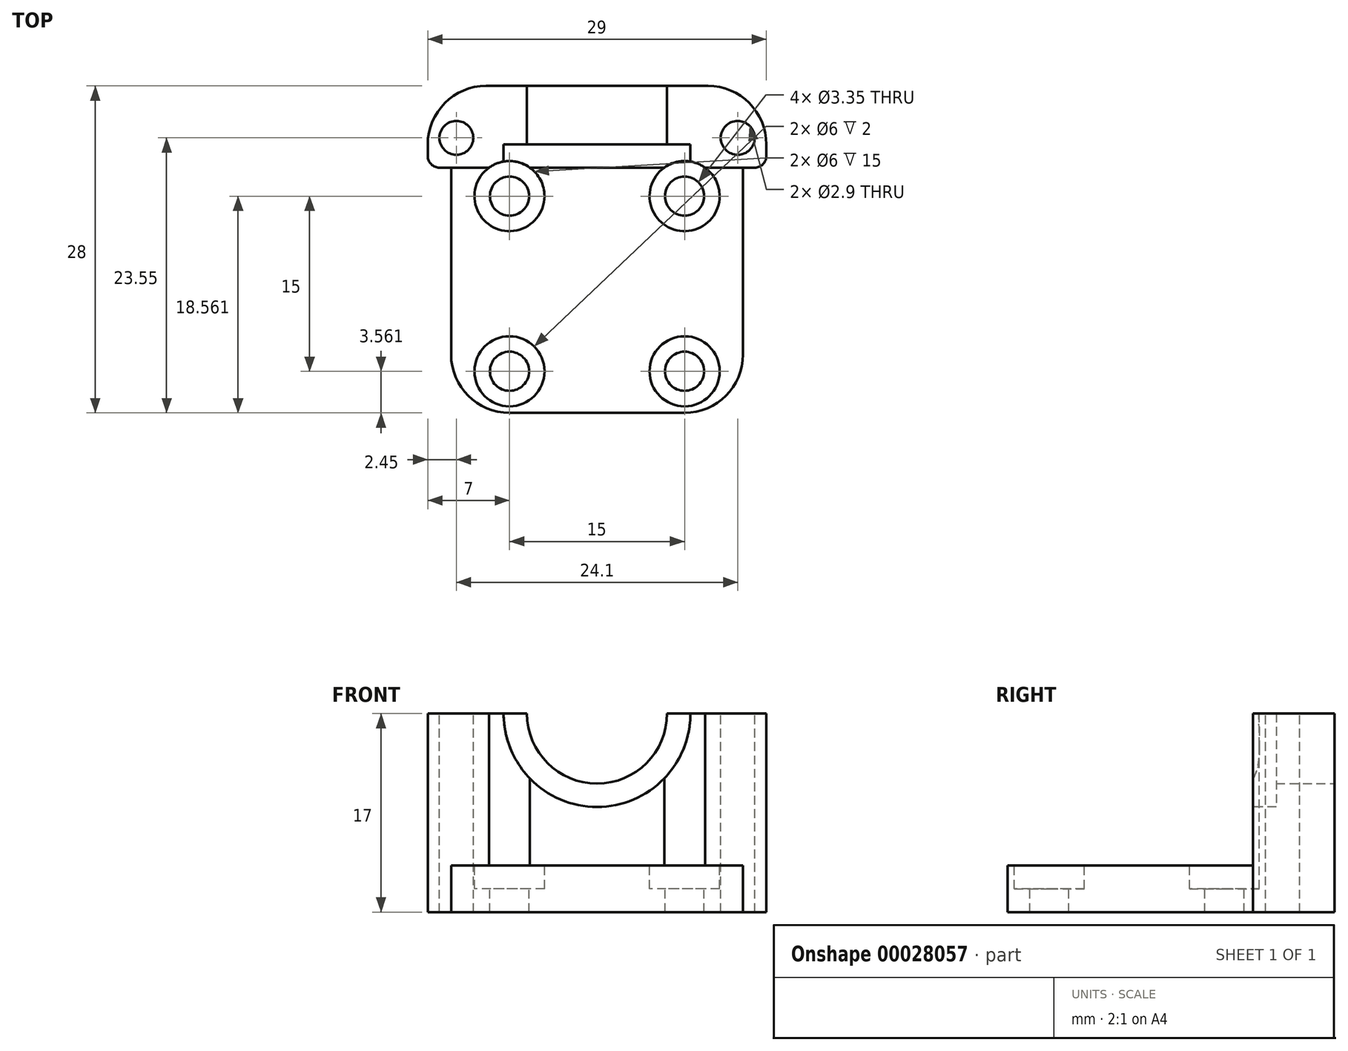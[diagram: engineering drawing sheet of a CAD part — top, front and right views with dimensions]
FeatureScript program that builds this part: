
annotation { "Feature Type Name" : "Feature", "Feature Type Description" : "" }
export const myFeature = defineFeature(function(context is Context, id is Id, definition is map)
    precondition{}
    {
        {
            var Q0;
            Q0=qCreatedBy(makeId("Top.planeOp"),FACE);
            var sketch = newSketch(context, id + "F0", { "sketchPlane" : qUnion([Q0])});
            skLineSegment(sketch, "E0.bottom", {"start": v(0, 0) * mm, "end": v(25, 0) * mm});
            skLineSegment(sketch, "E0.top", {"start": v(0, 28) * mm, "end": v(25, 28) * mm});
            skLineSegment(sketch, "E0.left", {"start": v(0, 0) * mm, "end": v(0, 28) * mm});
            skLineSegment(sketch, "E0.right", {"start": v(25, 0) * mm, "end": v(25, 28) * mm});
            skSolve(sketch);
        }
        {
            var Q0;
            Q0=qSketchRegion(id+"F0",true);
            extrude(context, id + "F1", {"entities" : qUnion([Q0]), "depth" : 4 * mm});
        }
        {
            var Q0;
            Q0=makeQuery(id+"F1.opExtrude","CAP_FACE",FACE,{"disambiguationData":[OSD([sQuery(id+"F0.wireOp",EDGE,"E0.bottom"),sQuery(id+"F0.wireOp",EDGE,"E0.top"),sQuery(id+"F0.wireOp",EDGE,"E0.left"),sQuery(id+"F0.wireOp",EDGE,"E0.right")])],"isStart":false});
            var sketch = newSketch(context, id + "F2", { "sketchPlane" : qUnion([Q0])});
            skCircle(sketch, "E1", {"center": v(5, 18.56) * mm, "radius": 1.68 * mm});
            skCircle(sketch, "E2", {"center": v(20, 18.56) * mm, "radius": 1.68 * mm});
            skCircle(sketch, "E3", {"center": v(5, 3.56) * mm, "radius": 1.68 * mm});
            skCircle(sketch, "E4", {"center": v(20, 3.56) * mm, "radius": 1.68 * mm});
            skLineSegment(sketch, "E5", {"start": v(5, 18.56) * mm, "end": v(0, 18.56) * mm});
            skLineSegment(sketch, "E6", {"start": v(20, 3.56) * mm, "end": v(25, 3.56) * mm});
            skCircle(sketch, "E7", {"center": v(5, 18.56) * mm, "radius": 3 * mm});
            skCircle(sketch, "E8", {"center": v(20, 18.56) * mm, "radius": 3 * mm});
            skCircle(sketch, "E9", {"center": v(5, 3.56) * mm, "radius": 3 * mm});
            skCircle(sketch, "E10", {"center": v(20, 3.56) * mm, "radius": 3 * mm});
            skSolve(sketch);
        }
        {
            var Q0;
            Q0=makeQuery(id+"F2.imprint","IMPRINT",FACE,{"disambiguationData":[TD([[makeQuery(id+"F2.imprint","IMPRINT",EDGE,{"derivedFrom":sQuery(id+"F2.wireOp",EDGE,"E1")}),1.0]])]});
            var Q1;
            Q1=makeQuery(id+"F2.imprint","IMPRINT",FACE,{"disambiguationData":[TD([[makeQuery(id+"F2.imprint","IMPRINT",EDGE,{"derivedFrom":sQuery(id+"F2.wireOp",EDGE,"E2")}),1.0]])]});
            var Q2;
            Q2=makeQuery(id+"F2.imprint","IMPRINT",FACE,{"disambiguationData":[TD([[makeQuery(id+"F2.imprint","IMPRINT",EDGE,{"derivedFrom":sQuery(id+"F2.wireOp",EDGE,"E4")}),1.0]])]});
            var Q3;
            Q3=makeQuery(id+"F2.imprint","IMPRINT",FACE,{"disambiguationData":[TD([[makeQuery(id+"F2.imprint","IMPRINT",EDGE,{"derivedFrom":sQuery(id+"F2.wireOp",EDGE,"E3")}),1.0]])]});
            extrude(context, id + "F3", {"entities" : qUnion([Q0, Q1, Q2, Q3]), "operationType" : NewBodyOperationType.REMOVE, "oppositeDirection" : true, "depth" : 25 * mm});
        }
        {
            var Q0;
            Q0=makeQuery(id+"F1.opExtrude","CAP_FACE",FACE,{"disambiguationData":[OSD([sQuery(id+"F0.wireOp",EDGE,"E0.bottom"),sQuery(id+"F0.wireOp",EDGE,"E0.top"),sQuery(id+"F0.wireOp",EDGE,"E0.left"),sQuery(id+"F0.wireOp",EDGE,"E0.right")])],"isStart":false});
            var sketch = newSketch(context, id + "F4", { "sketchPlane" : qUnion([Q0])});
            skLineSegment(sketch, "E11.bottom", {"start": v(0, 28) * mm, "end": v(25, 28) * mm});
            skLineSegment(sketch, "E11.top", {"start": v(0, 21) * mm, "end": v(25, 21) * mm});
            skLineSegment(sketch, "E11.left", {"start": v(0, 28) * mm, "end": v(0, 21) * mm});
            skLineSegment(sketch, "E11.right", {"start": v(25, 28) * mm, "end": v(25, 21) * mm});
            skSolve(sketch);
        }
        {
            var Q0;
            Q0=qSketchRegion(id+"F4",true);
            extrude(context, id + "F5", {"entities" : qUnion([Q0]), "operationType" : NewBodyOperationType.ADD, "depth" : 13 * mm});
        }
        {
            var Q0;
            Q0=makeQuery(id+"F5.boolean.opBoolean","MERGE",FACE,{"derivedFrom":[makeQuery(id+"F1.opExtrude","SWEPT_FACE",FACE,{"disambiguationData":[OSD([sQuery(id+"F0.wireOp",EDGE,"E0.top")])]}),makeQuery(id+"F5.opExtrude","SWEPT_FACE",FACE,{"disambiguationData":[OSD([sQuery(id+"F4.wireOp",EDGE,"E11.bottom")])]})]});
            var sketch = newSketch(context, id + "F6", { "sketchPlane" : qUnion([Q0])});
            skCircle(sketch, "E12", {"center": v(-12.5, 17) * mm, "radius": 6 * mm});
            skSolve(sketch);
        }
        {
            var Q0;
            {var subQ0=makeQuery(id+"F5.opExtrude","CAP_EDGE",EDGE,{"disambiguationData":[OSD([sQuery(id+"F4.wireOp",EDGE,"E11.bottom")])],"isStart":false});var subQ1=sQuery(id+"F6.wireOp",EDGE,"E12");var subQ3=makeQuery(id+"F6.imprint","INTERSECT",VERTEX,{"disambiguationData":[OD(0.0)],"derivedFrom":[subQ0,subQ1]});Q0=makeQuery(id+"F6.imprint","IMPRINT",FACE,{"disambiguationData":[TD([[makeQuery(id+"F6.imprint","IMPRINT",EDGE,{"disambiguationData":[TD([[subQ3,1.0]])],"derivedFrom":subQ1}),1.0]])]});}
            extrude(context, id + "F7", {"entities" : qUnion([Q0]), "operationType" : NewBodyOperationType.REMOVE, "oppositeDirection" : true, "depth" : 6 * mm});
        }
        {
            var Q0;
            Q0=makeQuery(id+"F5.opExtrude","SWEPT_FACE",FACE,{"disambiguationData":[OSD([sQuery(id+"F4.wireOp",EDGE,"E11.top")])]});
            var sketch = newSketch(context, id + "F8", { "sketchPlane" : qUnion([Q0])});
            skCircle(sketch, "E13", {"center": v(12.5, 17) * mm, "radius": 8 * mm});
            skSolve(sketch);
        }
        {
            var Q0;
            Q0=qSketchRegion(id+"F8",true);
            extrude(context, id + "F9", {"entities" : qUnion([Q0]), "operationType" : NewBodyOperationType.REMOVE, "oppositeDirection" : true, "depth" : 2 * mm});
        }
        {
            var Q0;
            Q0=makeQuery(id+"F2.imprint","IMPRINT",FACE,{"disambiguationData":[TD([[makeQuery(id+"F2.imprint","IMPRINT",EDGE,{"derivedFrom":sQuery(id+"F2.wireOp",EDGE,"E1")}),-1.0]])]});
            var Q1;
            Q1=makeQuery(id+"F2.imprint","IMPRINT",FACE,{"disambiguationData":[TD([[makeQuery(id+"F2.imprint","IMPRINT",EDGE,{"derivedFrom":sQuery(id+"F2.wireOp",EDGE,"E2")}),-1.0]])]});
            var Q2;
            Q2=makeQuery(id+"F2.imprint","IMPRINT",FACE,{"disambiguationData":[TD([[makeQuery(id+"F2.imprint","IMPRINT",EDGE,{"derivedFrom":sQuery(id+"F2.wireOp",EDGE,"E4")}),-1.0]])]});
            var Q3;
            Q3=makeQuery(id+"F2.imprint","IMPRINT",FACE,{"disambiguationData":[TD([[makeQuery(id+"F2.imprint","IMPRINT",EDGE,{"derivedFrom":sQuery(id+"F2.wireOp",EDGE,"E3")}),-1.0]])]});
            extrude(context, id + "F10", {"entities" : qUnion([Q0, Q1, Q2, Q3]), "operationType" : NewBodyOperationType.REMOVE, "oppositeDirection" : true, "depth" : 2 * mm});
        }
        {
            var Q0;
            Q0=makeQuery(id+"F1.opExtrude","SWEPT_EDGE",EDGE,{"disambiguationData":[OSD([sQuery(id+"F0.wireOp",EDGE,"E0.bottom"),sQuery(id+"F0.wireOp",EDGE,"E0.left")])]});
            var Q1;
            Q1=makeQuery(id+"F1.opExtrude","SWEPT_EDGE",EDGE,{"disambiguationData":[OSD([sQuery(id+"F0.wireOp",EDGE,"E0.bottom"),sQuery(id+"F0.wireOp",EDGE,"E0.right")])]});
            fillet(context, id + "F11", {"entities" : qUnion([Q0, Q1]), "radius" : 5 * mm, "tangentPropagation" : true, "allowEdgeOverflow" : false});
        }
        {
            var Q0;
            Q0=makeQuery(id+"F5.boolean.opBoolean","MERGE",FACE,{"derivedFrom":[makeQuery(id+"F1.opExtrude","SWEPT_FACE",FACE,{"disambiguationData":[OSD([sQuery(id+"F0.wireOp",EDGE,"E0.left")])]}),makeQuery(id+"F5.opExtrude","SWEPT_FACE",FACE,{"disambiguationData":[OSD([sQuery(id+"F4.wireOp",EDGE,"E11.left")])]})]});
            var sketch = newSketch(context, id + "F12", { "sketchPlane" : qUnion([Q0])});
            skLineSegment(sketch, "E14.bottom", {"start": v(-28, 0) * mm, "end": v(-21, 0) * mm});
            skLineSegment(sketch, "E14.top", {"start": v(-28, 17) * mm, "end": v(-21, 17) * mm});
            skLineSegment(sketch, "E14.left", {"start": v(-28, 0) * mm, "end": v(-28, 17) * mm});
            skLineSegment(sketch, "E14.right", {"start": v(-21, 0) * mm, "end": v(-21, 17) * mm});
            skSolve(sketch);
        }
        {
            var Q0;
            Q0=qSketchRegion(id+"F12",true);
            extrude(context, id + "F13", {"entities" : qUnion([Q0]), "operationType" : NewBodyOperationType.ADD, "depth" : 2 * mm});
        }
        {
            var Q0;
            Q0=makeQuery(id+"F5.boolean.opBoolean","MERGE",FACE,{"derivedFrom":[makeQuery(id+"F1.opExtrude","SWEPT_FACE",FACE,{"disambiguationData":[OSD([sQuery(id+"F0.wireOp",EDGE,"E0.right")])]}),makeQuery(id+"F5.opExtrude","SWEPT_FACE",FACE,{"disambiguationData":[OSD([sQuery(id+"F4.wireOp",EDGE,"E11.right")])]})]});
            var sketch = newSketch(context, id + "F14", { "sketchPlane" : qUnion([Q0])});
            skLineSegment(sketch, "E15.bottom", {"start": v(28, 0) * mm, "end": v(21, 0) * mm});
            skLineSegment(sketch, "E15.top", {"start": v(28, 17) * mm, "end": v(21, 17) * mm});
            skLineSegment(sketch, "E15.left", {"start": v(28, 0) * mm, "end": v(28, 17) * mm});
            skLineSegment(sketch, "E15.right", {"start": v(21, 0) * mm, "end": v(21, 17) * mm});
            skSolve(sketch);
        }
        {
            var Q0;
            Q0=qSketchRegion(id+"F14",true);
            extrude(context, id + "F15", {"entities" : qUnion([Q0]), "operationType" : NewBodyOperationType.ADD, "depth" : 2 * mm});
        }
        {
            var Q0;
            {var subQ0=sQuery(id+"F4.wireOp",EDGE,"E11.bottom");var subQ1=sQuery(id+"F4.wireOp",EDGE,"E11.top");var subQ2=sQuery(id+"F4.wireOp",EDGE,"E11.left");Q0=makeQuery(id+"F9.boolean.opBoolean","SPLIT",FACE,{"disambiguationData":[TD([makeQuery(id+"F1.opExtrude","SWEPT_FACE",FACE,{"disambiguationData":[OSD([sQuery(id+"F0.wireOp",EDGE,"E0.left")])]})])],"derivedFrom":makeQuery(id+"F5.opExtrude","CAP_FACE",FACE,{"disambiguationData":[OSD([subQ0,subQ1,subQ2,sQuery(id+"F4.wireOp",EDGE,"E11.right")])],"isStart":false})});}
            var sketch = newSketch(context, id + "F16", { "sketchPlane" : qUnion([Q0])});
            skCircle(sketch, "E16", {"center": v(0.45, 23.55) * mm, "radius": 1.45 * mm});
            skCircle(sketch, "E17", {"center": v(24.55, 23.55) * mm, "radius": 1.45 * mm});
            skSolve(sketch);
        }
        {
            var Q0;
            Q0=qSketchRegion(id+"F16",true);
            extrude(context, id + "F17", {"entities" : qUnion([Q0]), "operationType" : NewBodyOperationType.REMOVE, "oppositeDirection" : true, "depth" : 25 * mm});
        }
        {
            var Q0;
            Q0=makeQuery(id+"F13.opExtrude","CAP_EDGE",EDGE,{"disambiguationData":[OSD([sQuery(id+"F12.wireOp",EDGE,"E14.left")])],"isStart":false});
            var Q1;
            Q1=makeQuery(id+"F15.opExtrude","CAP_EDGE",EDGE,{"disambiguationData":[OSD([sQuery(id+"F14.wireOp",EDGE,"E15.left")])],"isStart":false});
            fillet(context, id + "F18", {"entities" : qUnion([Q0, Q1]), "radius" : 5 * mm, "tangentPropagation" : true, "allowEdgeOverflow" : false});
        }
        {
            var Q0;
            Q0=makeQuery(id+"F1.opExtrude","CAP_FACE",FACE,{"disambiguationData":[OSD([sQuery(id+"F0.wireOp",EDGE,"E0.bottom"),sQuery(id+"F0.wireOp",EDGE,"E0.top"),sQuery(id+"F0.wireOp",EDGE,"E0.left"),sQuery(id+"F0.wireOp",EDGE,"E0.right")])],"isStart":false});
            var sketch = newSketch(context, id + "F19", { "sketchPlane" : qUnion([Q0])});
            skCircle(sketch, "E18.0", {"center": v(5, 18.56) * mm, "radius": 3 * mm});
            skCircle(sketch, "E19.0", {"center": v(20, 18.56) * mm, "radius": 3 * mm});
            skSolve(sketch);
        }
        {
            var Q0;
            Q0 = qSketchRegion(id + "F19", true);
            extrude(context, id + "F20", {"entities" : qUnion([Q0]), "operationType" : NewBodyOperationType.REMOVE, "depth" : 25 * mm});
        }
        {
            var Q0;
            Q0=makeQuery(id+"F15.opExtrude","CAP_EDGE",EDGE,{"disambiguationData":[OSD([sQuery(id+"F14.wireOp",EDGE,"E15.right")])],"isStart":false});
            var Q1;
            Q1=makeQuery(id+"F13.opExtrude","CAP_EDGE",EDGE,{"disambiguationData":[OSD([sQuery(id+"F12.wireOp",EDGE,"E14.right")])],"isStart":false});
            fillet(context, id + "F21", {"entities" : qUnion([Q0, Q1]), "radius" : 1 * mm, "tangentPropagation" : true, "allowEdgeOverflow" : false});
        }
    });
